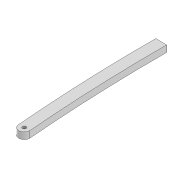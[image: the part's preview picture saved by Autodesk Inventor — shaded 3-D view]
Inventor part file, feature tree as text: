
AUTODESK INVENTOR PART (.ipt)
format: ipt  version: 2022 (Build 260153000, 153)  size: 104,960 bytes
history: native  units: mm
features: extrude x2, sketch x1
ambient origin geometry x8: Origin, YZ Plane, XZ Plane, XY Plane, X Axis, Y Axis, Z Axis, Center Point
bodies: Solid1 (feature_tree)
feature tree (3):
  extrude  "Extrusion1"  Depth=10.0mm
  extrude  "Extrusion2"  Depth=10.0mm
  sketch  "Sketch2"  dims[d0=3.3mm d1=3.3mm d2=10.0mm d3=253.429mm d6=6.0mm d7=0.0mm d16=1500.0mm d17=1500.0mm d18=3.3mm d19=112.0mm d20=10.0mm d21=0.0mm]
